# Revit family: Shelters_CityScapes_Cantilever-Canopy---1
name_source: partatom
category: Specialty Equipment
units: mm (PartAtom-declared; Revit-internal decimal feet)

## family parameters
Cut with Voids When Loaded = No
Enable Cutting in Views = Yes
Host = Face
Maintain Annotation Orientation = No
OmniClass Number = 23.30.60.11.11.11
Part Type = Normal
Room Calculation Point = No
Round Connector Dimension = Use Diameter
Shared = No

## types (1)
- Cantilever Canopy
    Assembly Code = B2010
    Default Elevation = 120"
    Description = With clean geometry and a visually weightless form, Cantilever Canopies & Awnings bring refined elegance to any exterior. Their crisp, horizontal lines appear to hover, creating a bold architectural statement with minimal visual weight. Built for longevity and designed to impress, they offer a striking blend of simplicity, sophistication, and lasting performance.
    Keynote = 07 71 00
    Manufacturer = CityScapes® International, Inc.
    Model = Cantilever Canopy
    Product Documentation Link = https://cityscapesinc.com
    Product Page URL = https://cityscapesinc.com
    URL = https://cityscapesinc.com
    Version = 1

## geometry (parser evidence)
native form markers: Sweep x3
no freeform markers — native parametric forms only
